# Revit family: 110104-00034 Камера оптическая трубопроводная КОТ-2-ССД
name_source: partatom
category: Обобщенные модели
units: mm (PartAtom-declared; Revit-internal decimal feet)

## family parameters
Всегда вертикально = Да
Может служить основой для арматурных стержней = Нет
На основе рабочей плоскости = Нет
Общий = Нет
При загрузке вырезать с полостями = Нет
Размер круглого соединителя = Использовать диаметр
Тип детали = Нормальный
Точка расчета площади = Нет

## types (1)
- Камера оптическая трубопроводная КОТ-2-ССД
    ADSK_Cертификат соответствия = https://www.ssd.ru
    ADSK_Высота = 495 мм
    ADSK_Длина = 1070 мм
    ADSK_Длина2 = 1000 мм
    ADSK_Изготовитель = АО "СВЯЗЬСТРОЙДЕТАЛЬ"
    ADSK_Код изделия = 110104-00034
    ADSK_Марка = Камеры оптические трубопроводные
    ADSK_Масса = 33
    ADSK_Материал = Полиэтилен среднего давления
    ADSK_Наименование = Камера оптическая трубопроводная КОТ-2-ССД
    ADSK_Ссылка на сайт = https://www.ssd.ru
    ADSK_Ширина = 1070 мм
    ADSK_Ширина2 = 730 мм
